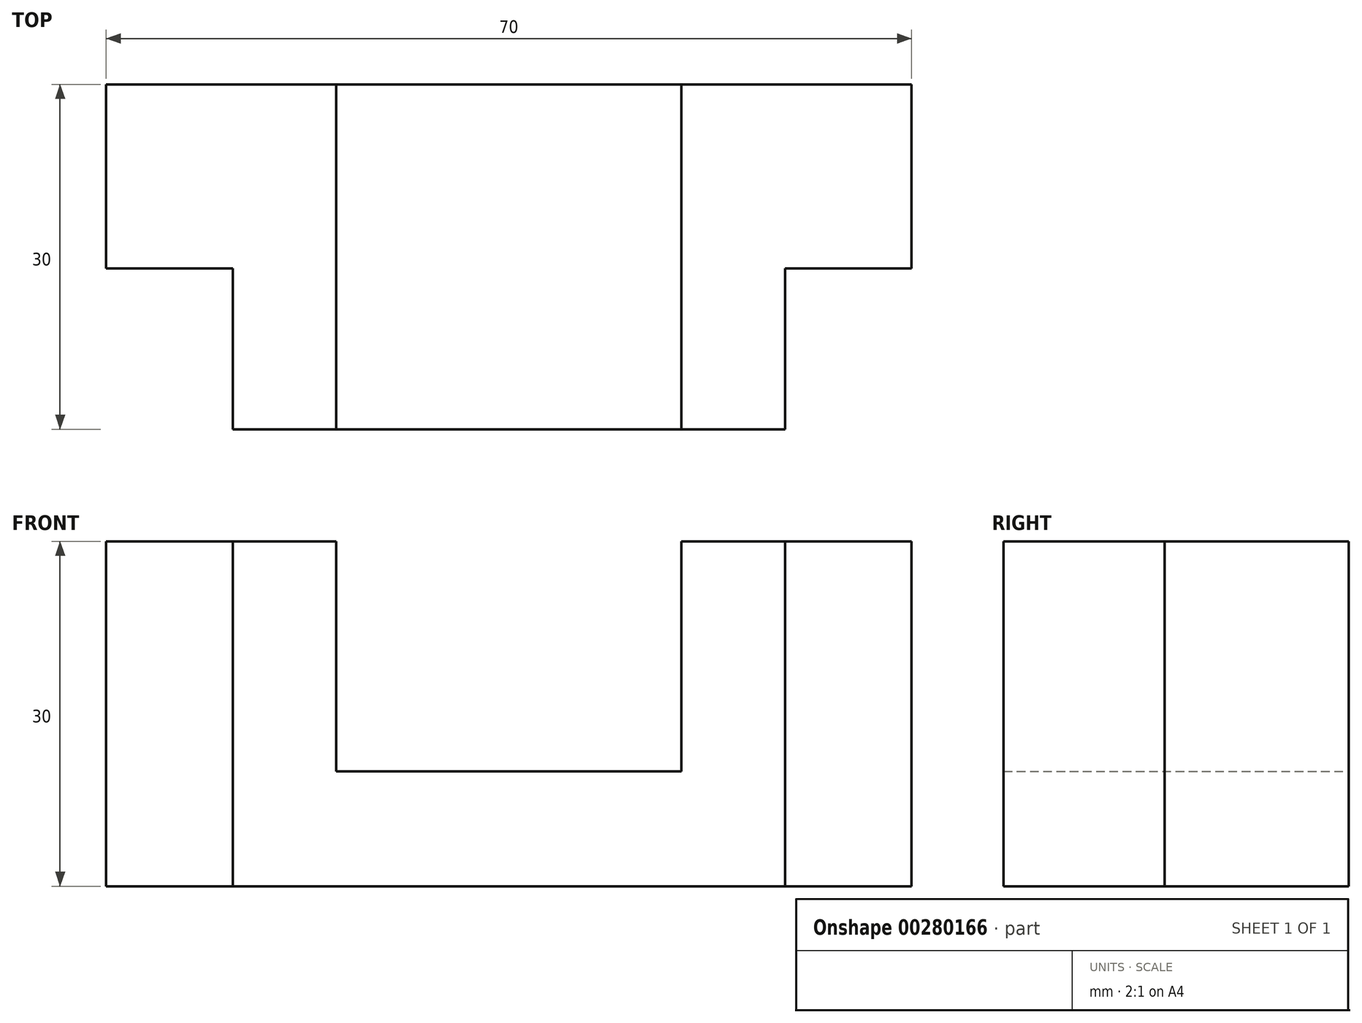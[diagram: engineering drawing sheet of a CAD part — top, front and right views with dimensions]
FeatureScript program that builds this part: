
annotation { "Feature Type Name" : "Feature", "Feature Type Description" : "" }
export const myFeature = defineFeature(function(context is Context, id is Id, definition is map)
    precondition{}
    {
        {
            var Q0;
            Q0=qCreatedBy(makeId("Front.planeOp"),FACE);
            var sketch = newSketch(context, id + "F0", { "sketchPlane" : qUnion([Q0])});
            skLineSegment(sketch, "E0", {"start": v(-35, 10.64) * mm, "end": v(-15, 10.64) * mm});
            skLineSegment(sketch, "E1", {"start": v(-15, 10.64) * mm, "end": v(-15, -9.36) * mm});
            skLineSegment(sketch, "E2", {"start": v(-15, -9.36) * mm, "end": v(15, -9.36) * mm});
            skLineSegment(sketch, "E3", {"start": v(15, -9.36) * mm, "end": v(15, 10.64) * mm});
            skLineSegment(sketch, "E4", {"start": v(15, 10.64) * mm, "end": v(35, 10.64) * mm});
            skLineSegment(sketch, "E5", {"start": v(35, 10.64) * mm, "end": v(35, -19.36) * mm});
            skLineSegment(sketch, "E6", {"start": v(35, -19.36) * mm, "end": v(-35, -19.36) * mm});
            skLineSegment(sketch, "E7", {"start": v(-35, -19.36) * mm, "end": v(-35, 10.64) * mm});
            skSolve(sketch);
        }
        {
            var Q0;
            Q0=makeQuery(id+"F0.imprint","IMPRINT",FACE,{"disambiguationData":[TD([[makeQuery(id+"F0.imprint","IMPRINT",EDGE,{"derivedFrom":sQuery(id+"F0.wireOp",EDGE,"E0")}),-1.0]])]});
            extrude(context, id + "F1", {"entities" : qUnion([Q0]), "depth" : 30 * mm});
        }
        {
            var Q0;
            Q0=qCreatedBy(makeId("Top.planeOp"),FACE);
            var sketch = newSketch(context, id + "F2", { "sketchPlane" : qUnion([Q0])});
            skLineSegment(sketch, "E8", {"start": v(-35, -16) * mm, "end": v(-24, -16) * mm});
            skLineSegment(sketch, "E9", {"start": v(-24, -16) * mm, "end": v(-24, -30) * mm});
            skLineSegment(sketch, "E10", {"start": v(-35, -16) * mm, "end": v(-35, -30) * mm});
            skLineSegment(sketch, "E11", {"start": v(-35, -30) * mm, "end": v(-24, -30) * mm});
            skLineSegment(sketch, "E12.MirrorCS", {"start": v(24, -16) * mm, "end": v(24, -30) * mm});
            skLineSegment(sketch, "E13.MirrorCS", {"start": v(35, -16) * mm, "end": v(24, -16) * mm});
            skLineSegment(sketch, "E14.MirrorCS", {"start": v(35, -16) * mm, "end": v(35, -30) * mm});
            skLineSegment(sketch, "E15.MirrorCS", {"start": v(35, -30) * mm, "end": v(24, -30) * mm});
            skSolve(sketch);
        }
        {
            var Q0;
            Q0 = qSketchRegion(id + "F2", true);
            extrude(context, id + "F3", {"entities" : qUnion([Q0]), "operationType" : NewBodyOperationType.REMOVE, "endBound" : BoundingType.SYMMETRIC, "oppositeDirection" : true, "depth" : 40 * mm});
        }
    });
